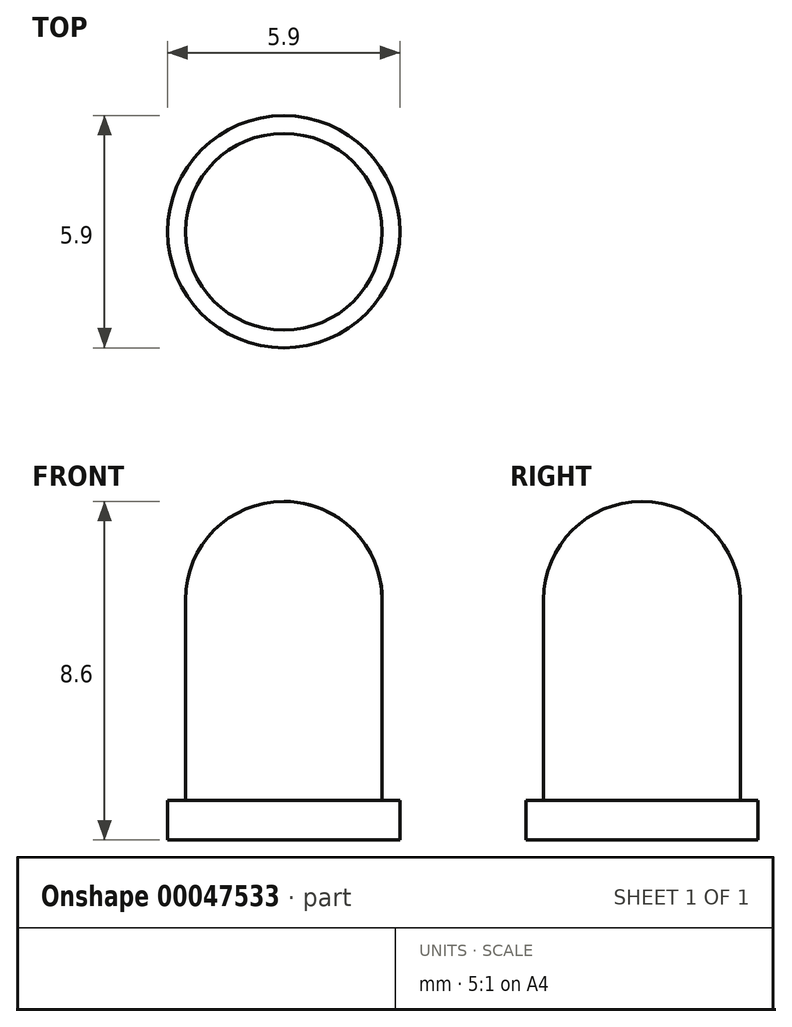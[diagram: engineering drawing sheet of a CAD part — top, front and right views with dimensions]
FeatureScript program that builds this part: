
annotation { "Feature Type Name" : "Feature", "Feature Type Description" : "" }
export const myFeature = defineFeature(function(context is Context, id is Id, definition is map)
    precondition{}
    {
        {
            var Q0;
            Q0=qCreatedBy(makeId("Top.planeOp"),FACE);
            var sketch = newSketch(context, id + "F0", { "sketchPlane" : qUnion([Q0])});
            skCircle(sketch, "E0", {"center": v(0, 0) * mm, "radius": 2.5 * mm});
            skSolve(sketch);
        }
        {
            var Q0;
            Q0 = qSketchRegion(id + "F0", true);
            extrude(context, id + "F1", {"entities" : qUnion([Q0]), "depth" : 8.6 * mm});
        }
        {
            var Q0;
            Q0=makeQuery(id+"F1.opExtrude","CAP_FACE",FACE,{"disambiguationData":[OSD([sQuery(id+"F0.wireOp",EDGE,"E0")])],"isStart":false});
            fillet(context, id + "F2", {"entities" : qUnion([Q0]), "radius" : 2.5 * mm, "tangentPropagation" : true, "allowEdgeOverflow" : false});
        }
        {
            var Q0;
            Q0=makeQuery(id+"F1.opExtrude","CAP_FACE",FACE,{"disambiguationData":[OSD([sQuery(id+"F0.wireOp",EDGE,"E0")])],"isStart":true});
            var sketch = newSketch(context, id + "F3", { "sketchPlane" : qUnion([Q0])});
            skCircle(sketch, "E1", {"center": v(0, 0) * mm, "radius": 2.95 * mm});
            skSolve(sketch);
        }
        {
            var Q0;
            Q0 = qSketchRegion(id + "F3", true);
            extrude(context, id + "F4", {"entities" : qUnion([Q0]), "operationType" : NewBodyOperationType.ADD, "oppositeDirection" : true, "depth" : 1 * mm});
        }
    });
